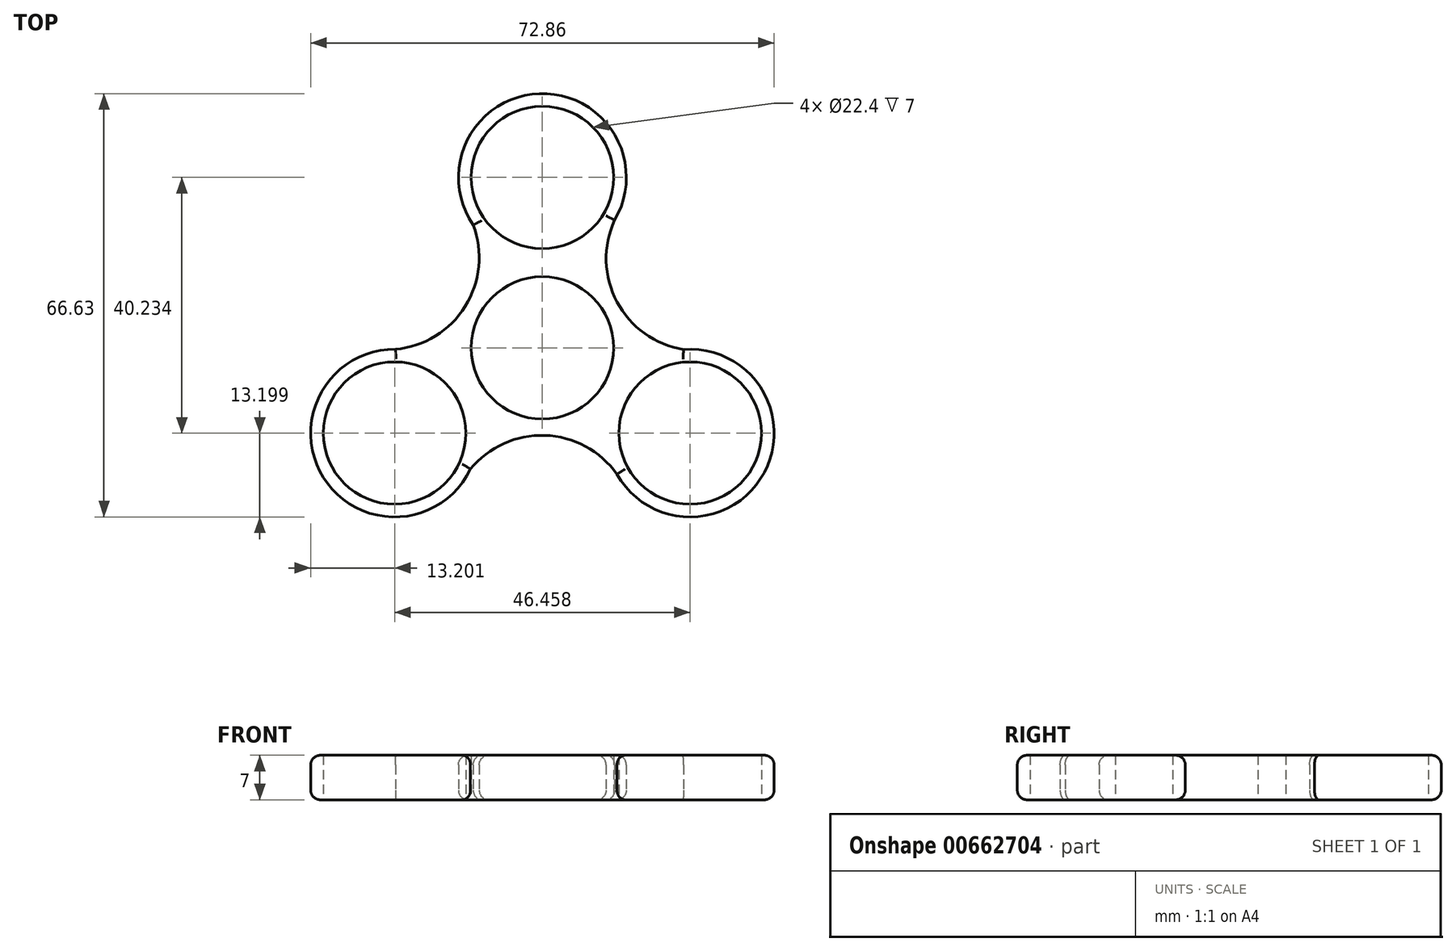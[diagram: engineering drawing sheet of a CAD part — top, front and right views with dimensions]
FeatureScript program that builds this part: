
annotation { "Feature Type Name" : "Feature", "Feature Type Description" : "" }
export const myFeature = defineFeature(function(context is Context, id is Id, definition is map)
    precondition{}
    {
        {
            var Q0;
            Q0=qCreatedBy(makeId("Top.planeOp"),FACE);
            var sketch = newSketch(context, id + "F0", { "sketchPlane" : qUnion([Q0])});
            skCircle(sketch, "E0", {"center": v(0, 0) * mm, "radius": 11.2 * mm});
            skCircle(sketch, "E1", {"center": v(0, 26.82) * mm, "radius": 11.2 * mm});
            skArc(sketch, "E2", {"start": v(11.36, 20.1) * mm, "mid": v(-0.45, 40.01) * mm, "end": v(-10.87, 19.34) * mm});
            skCircle(sketch, "E3.1.0", {"center": v(-23.23, -13.41) * mm, "radius": 11.2 * mm});
            skArc(sketch, "E3.1.1", {"start": v(-23.08, -0.21) * mm, "mid": v(-34.43, -20.4) * mm, "end": v(-11.3, -19.08) * mm});
            skCircle(sketch, "E3.2.0", {"center": v(23.23, -13.41) * mm, "radius": 11.2 * mm});
            skArc(sketch, "E3.2.1", {"start": v(11.72, -19.88) * mm, "mid": v(34.88, -19.62) * mm, "end": v(22.18, -0.25) * mm});
            skArc(sketch, "E4", {"start": v(11.36, 20.1) * mm, "mid": v(11.73, 7.24) * mm, "end": v(22.18, -0.25) * mm});
            skArc(sketch, "E5.1.0", {"start": v(-23.08, -0.21) * mm, "mid": v(-12.13, 6.54) * mm, "end": v(-10.87, 19.34) * mm});
            skArc(sketch, "E5.2.0", {"start": v(11.72, -19.88) * mm, "mid": v(0.4, -13.77) * mm, "end": v(-11.3, -19.08) * mm});
            skSolve(sketch);
        }
        {
            var Q0;
            Q0=makeQuery(id+"F0.imprint","IMPRINT",FACE,{"disambiguationData":[TD([[makeQuery(id+"F0.imprint","IMPRINT",EDGE,{"derivedFrom":sQuery(id+"F0.wireOp",EDGE,"E0")}),-1.0]])]});
            extrude(context, id + "F1", {"entities" : qUnion([Q0]), "depth" : 7 * mm, "offsetDistance" : 25 * mm});
        }
        {
            var Q0;
            Q0=makeQuery(id+"F1.opExtrude","CAP_EDGE",EDGE,{"disambiguationData":[OSD([sQuery(id+"F0.wireOp",EDGE,"E5.2.0")])],"isStart":false});
            var Q1;
            Q1=makeQuery(id+"F1.opExtrude","CAP_EDGE",EDGE,{"disambiguationData":[OSD([sQuery(id+"F0.wireOp",EDGE,"E3.1.1")])],"isStart":false});
            var Q2;
            Q2=makeQuery(id+"F1.opExtrude","CAP_EDGE",EDGE,{"disambiguationData":[OSD([sQuery(id+"F0.wireOp",EDGE,"E5.2.0")])],"isStart":true});
            var Q3;
            Q3=makeQuery(id+"F1.opExtrude","CAP_EDGE",EDGE,{"disambiguationData":[OSD([sQuery(id+"F0.wireOp",EDGE,"E5.1.0")])],"isStart":false});
            var Q4;
            Q4=makeQuery(id+"F1.opExtrude","CAP_EDGE",EDGE,{"disambiguationData":[OSD([sQuery(id+"F0.wireOp",EDGE,"E2")])],"isStart":false});
            var Q5;
            Q5=makeQuery(id+"F1.opExtrude","CAP_EDGE",EDGE,{"disambiguationData":[OSD([sQuery(id+"F0.wireOp",EDGE,"E4")])],"isStart":false});
            var Q6;
            Q6=makeQuery(id+"F1.opExtrude","CAP_EDGE",EDGE,{"disambiguationData":[OSD([sQuery(id+"F0.wireOp",EDGE,"E3.2.1")])],"isStart":false});
            fillet(context, id + "F2", {"entities" : qUnion([Q0, Q1, Q2, Q3, Q4, Q5, Q6]), "radius" : 1.5 * mm, "tangentPropagation" : true, "allowEdgeOverflow" : false});
        }
        {
            var Q0;
            Q0=makeQuery(id+"F1.opExtrude","CAP_EDGE",EDGE,{"disambiguationData":[OSD([sQuery(id+"F0.wireOp",EDGE,"E2")])],"isStart":true});
            var Q1;
            Q1=makeQuery(id+"F1.opExtrude","CAP_EDGE",EDGE,{"disambiguationData":[OSD([sQuery(id+"F0.wireOp",EDGE,"E4")])],"isStart":true});
            var Q2;
            Q2=makeQuery(id+"F1.opExtrude","CAP_EDGE",EDGE,{"disambiguationData":[OSD([sQuery(id+"F0.wireOp",EDGE,"E5.1.0")])],"isStart":true});
            var Q3;
            Q3=makeQuery(id+"F1.opExtrude","CAP_EDGE",EDGE,{"disambiguationData":[OSD([sQuery(id+"F0.wireOp",EDGE,"E3.1.1")])],"isStart":true});
            var Q4;
            {var subQ0=sQuery(id+"F0.wireOp",EDGE,"E5.2.0");Q4=makeQuery(id+"F2.opFillet","BLEND_EDGE",EDGE,{"blendedFrom":[makeQuery(id+"F1.opExtrude","CAP_EDGE",EDGE,{"disambiguationData":[OSD([subQ0])],"isStart":true}),makeQuery(id+"F1.opExtrude","SWEPT_FACE",FACE,{"disambiguationData":[OSD([subQ0])]})],"blendedInto":[makeQuery(id+"F1.opExtrude","SWEPT_FACE",FACE,{"disambiguationData":[OSD([subQ0])]})]});}
            var Q5;
            Q5=makeQuery(id+"F1.opExtrude","CAP_EDGE",EDGE,{"disambiguationData":[OSD([sQuery(id+"F0.wireOp",EDGE,"E3.2.1")])],"isStart":true});
            fillet(context, id + "F3", {"entities" : qUnion([Q0, Q1, Q2, Q3, Q4, Q5]), "radius" : 1.5 * mm, "tangentPropagation" : true, "allowEdgeOverflow" : false});
        }
    });
